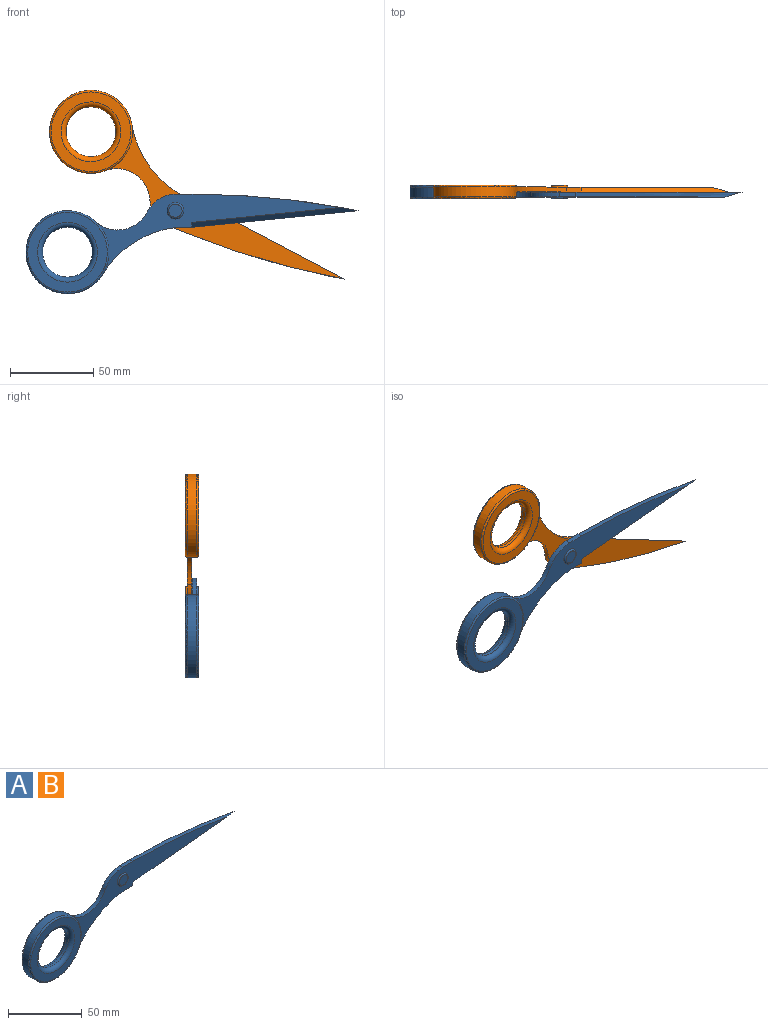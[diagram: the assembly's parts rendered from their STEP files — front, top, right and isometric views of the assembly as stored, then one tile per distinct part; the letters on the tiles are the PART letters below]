
ASSEMBLY  parts=2 mates=1
PART A: 20 faces, bbox 202.1x8x62.1 mm
  f0: plane 147.92x48.21mm, normal (0,-1,0), area 1657.5mm2, adj f2,f3,f4,f5,f6,f7,f13,f14
  f1: plane 158.22x48.21mm, normal (0,1,0), area 2020.8mm2, adj f2,f3,f4,f5,f6,f7,f8,f13
  f2: plane 10x3mm, normal (0,0,1), area 30mm2, adj f0,f1,f4,f6
  f3: plane 9.4x3mm, normal (0,0,-1), area 28.2mm2, adj f0,f1,f5,f14
  f4: cylinder r=505mm len=100mm, axis (0,1,0), area 286.4mm2, adj f0,f1,f2,f13
  f5: cylinder r=60.69mm len=44.37mm, axis (0,1,0), area 163.1mm2, adj f0,f1,f3,f8
  f6: cylinder r=20mm len=16.62mm, axis (0,1,0), area 60.8mm2, adj f0,f1,f2,f7
  f7: cylinder r=20mm len=31.6mm, axis (0,1,0), area 112.5mm2, adj f0,f1,f6,f8
  f8: cylinder r=25mm len=50mm, axis (0,1,0), area 838.1mm2, adj f1,f5,f7,f18,f19
  f9: plane 48x48mm, normal (0,1,0), area 791.7mm2, adj f15,f18
  f10: cylinder r=15mm len=30mm, axis (0,1,0), area 188.5mm2, adj f15,f16
  f11: plane 48x48mm, normal (0,-1,0), area 791.7mm2, adj f16,f19
  f12: plane 8x8mm, normal (0,-1,0), area 50.3mm2, adj f17
  f13: plane 100x11.97mm, normal (0.07,-0.71,-0.71), area 403.7mm2, adj f0,f1,f4,f14
  f14: plane 3x3mm, normal (1,0,0), area 4.5mm2, adj f0,f3,f13
  f15: torus R=18mm, axis (0,-1,0), area 476.4mm2, adj f9,f10
  f16: torus R=18mm, axis (0,-1,0), area 476.4mm2, adj f10,f11
  f17: torus R=4mm, axis (0,-1,0), area 45.8mm2, adj f0,f12
  f18: torus R=24mm, axis (0,-1,0), area 243.2mm2, adj f8,f9
  f19: torus R=24mm, axis (0,-1,0), area 243.2mm2, adj f0,f8,f11
PART B: same geometry as A
PLACE A t=(-48.23,-20.5,22.35)mm fixed
PLACE B rot(axis=(0.98,0,-0.19),180deg) t=(-48.23,-20.5,22.35)mm
MATE revolute A.f17 <-> B.f17  axis (0,-1,0) through (-48.23,-20.5,22.35)mm
